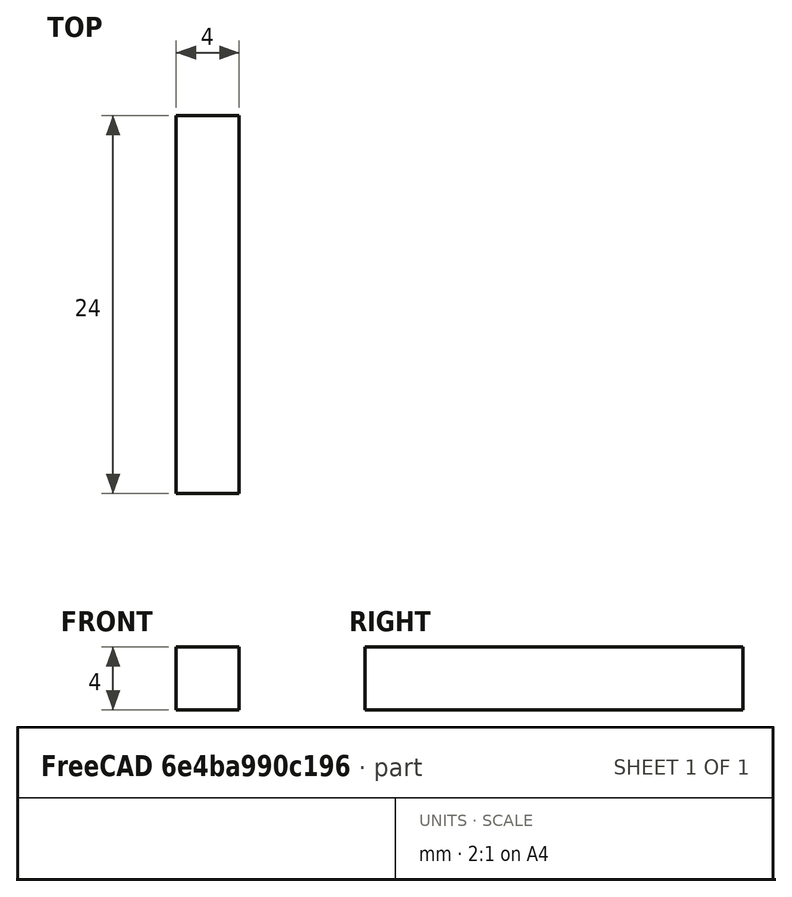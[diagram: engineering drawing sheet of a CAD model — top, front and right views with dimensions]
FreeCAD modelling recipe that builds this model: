
FCSTD DOCUMENT  (FreeCAD 1.0R39285 (Git))
Label: bottom-pin-01
License: All rights reserved
LicenseURL: http://en.wikipedia.org/wiki/All_rights_reserved
objects: Sketcher::SketchObject×1, PartDesign::Pad×1, PartDesign::Body×1, App::Part×1
note: 6 computed .brp shape members not serialized (recipe doc carries the construction recipe); baked Part::Feature solids carry a one-line shape summary decoded from their .brp

FEATURE [Sketcher::SketchObject] Sketch001
  ArcFitTolerance = 1e-06
  FullyConstrained = true
  MakeInternals = false
  MapMode = 45
  Placement = pos=(-8.84591,-9.71239,7.5) rot=(-1,0,0;1.5708rad)
  sketch-geometry (6):
    g0: LineSegment StartX=-2.15409 StartY=-2 StartZ=0 EndX=1.84591 EndY=-2 EndZ=0
    g1: LineSegment StartX=1.84591 StartY=-2 StartZ=0 EndX=1.84591 EndY=2 EndZ=0
    g2: LineSegment StartX=1.84591 StartY=2 StartZ=0 EndX=-2.15409 EndY=2 EndZ=0
    g3: LineSegment StartX=-2.15409 StartY=2 StartZ=0 EndX=-2.15409 EndY=-2 EndZ=0
    g4: GeomPoint [constr] X=-0.154088 Y=8.69e-14 Z=0
    g5: GeomPoint [constr] X=-3.15409 Y=8.69e-14 Z=0
  constraints (14):
    c: Coincident(g0,g1)
    c: Coincident(g1,g2)
    c: Coincident(g2,g3)
    c: Coincident(g3,g0)
    c: Horizontal(g0)
    c: Horizontal(g2)
    c: Vertical(g1)
    c: Vertical(g3)
    c: Symmetric(g2,g0,g4)
    c: Distance(g1,g3) = 4
    c: Distance(g0,g2) = 4
    c: DistanceX(g4,g-5) = -3
    c: Symmetric(g-5,g-7,g5)
    c: DistanceY(g5,g4) = 0
FEATURE [PartDesign::Pad] Pad
  Direction = (0,1,2e-16)
  Length = 24
  Length2 = 10
  Placement = pos=(-8.84591,-9.71239,7.5) rot=(-1,0,0;1.5708rad)
  Profile = -> Sketch001
  ReferenceAxis = -> Sketch001 [N_Axis]
  Suppressed = false
  Type = 0
FEATURE [PartDesign::Body] Body
  AllowCompound = false
  Group = -> [Sketch001,Pad]
  Origin = -> Origin001
  Tip = -> Pad
FEATURE [App::Part] Part
  Group = -> [Body]
  Origin = -> Origin
